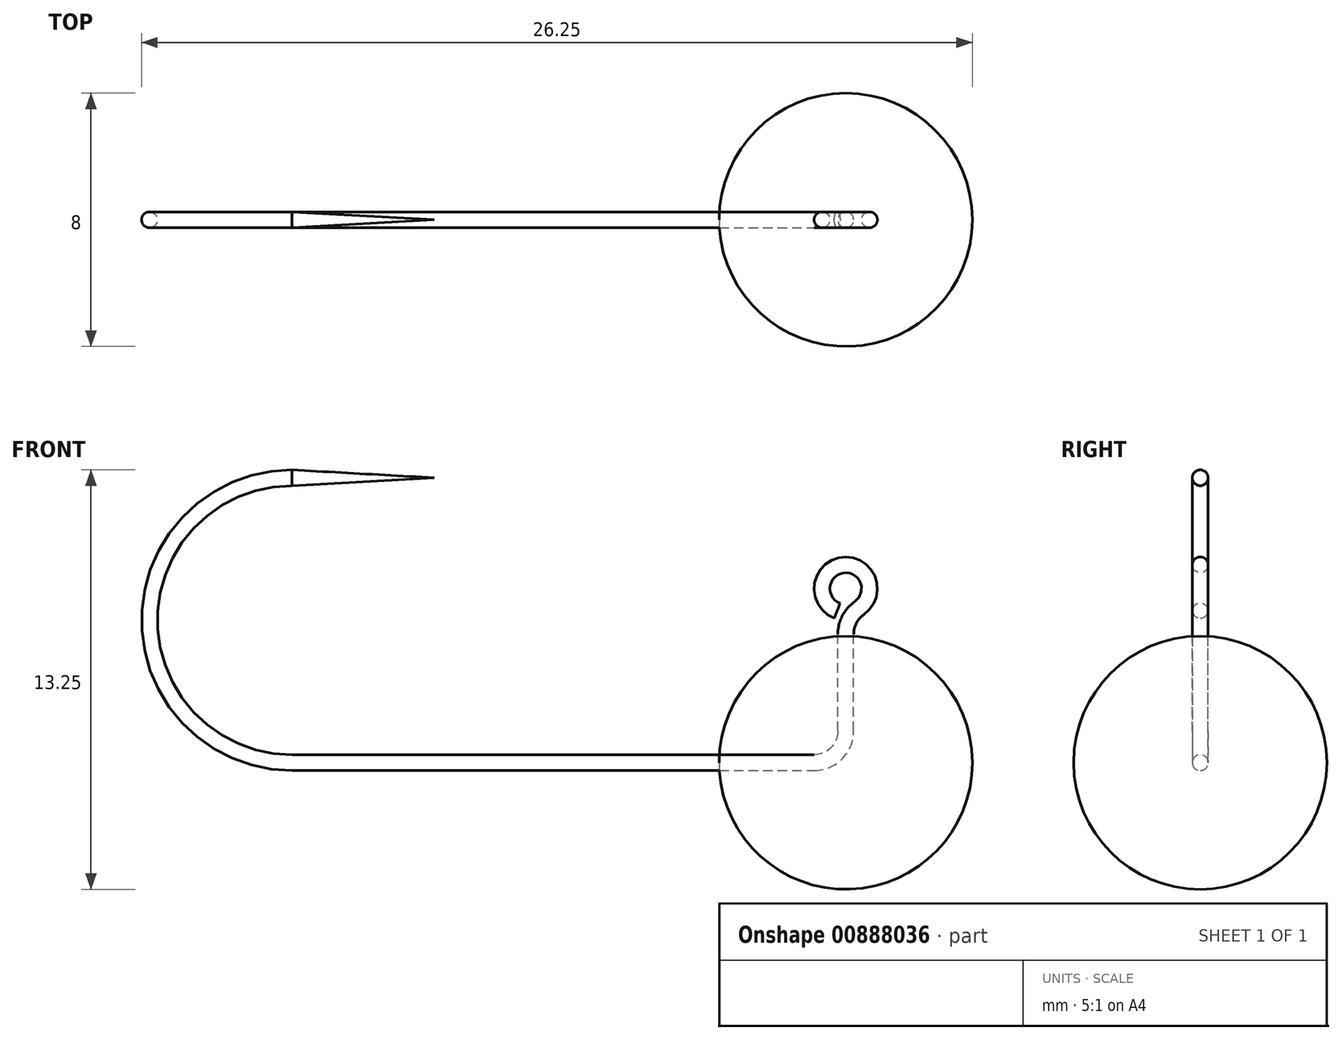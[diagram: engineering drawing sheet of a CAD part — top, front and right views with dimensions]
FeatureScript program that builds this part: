
annotation { "Feature Type Name" : "Feature", "Feature Type Description" : "" }
export const myFeature = defineFeature(function(context is Context, id is Id, definition is map)
    precondition{}
    {
        {
            var Q0;
            Q0=qCreatedBy(makeId("Front.planeOp"),FACE);
            var sketch = newSketch(context, id + "F0", { "sketchPlane" : qUnion([Q0])});
            skArc(sketch, "E0", {"start": v(4, 0) * mm, "mid": v(0, 4) * mm, "end": v(-4, 0) * mm});
            skLineSegment(sketch, "E1", {"start": v(-1, 0) * mm, "end": v(-17.5, 0) * mm});
            skArc(sketch, "E2", {"start": v(-17.5, 0) * mm, "mid": v(-22, 4.5) * mm, "end": v(-17.5, 9) * mm});
            skLineSegment(sketch, "E3", {"start": v(-17.5, 9) * mm, "end": v(-13, 9) * mm});
            skLineSegment(sketch, "E4", {"start": v(0, 1) * mm, "end": v(0, 4.06) * mm});
            skArc(sketch, "E5", {"start": v(0.43, 4.88) * mm, "mid": v(-0.09, 6.24) * mm, "end": v(-0.27, 4.8) * mm});
            skPoint(sketch, "E6.visualSharp", {"position": v(0, 4.75) * mm});
            skArc(sketch, "E6.filletArc", {"start": v(0.43, 4.88) * mm, "mid": v(0.11, 4.53) * mm, "end": v(0, 4.06) * mm});
            skArc(sketch, "E7.filletArc", {"start": v(-1, 0) * mm, "mid": v(-0.3, 0.3) * mm, "end": v(0, 1) * mm});
            skLineSegment(sketch, "E8", {"start": v(-4, 0) * mm, "end": v(4, 0) * mm});
            skSolve(sketch);
        }
        {
            var Q0;
            Q0=makeQuery(id+"F0.imprint","IMPRINT",FACE,{"disambiguationData":[TD([[makeQuery(id+"F0.imprint","IMPRINT",EDGE,{"derivedFrom":sQuery(id+"F0.wireOp",EDGE,"E0")}),1.0]])]});
            var Q1;
            Q1=sQuery(id+"F0.wireOp",EDGE,"E1");
            revolve(context, id + "F1", {"surfaceOperationType" : NewSurfaceOperationType.NEW, "entities" : qUnion([Q0]), "axis" : qUnion([Q1]), "revolveType" : RevolveType.FULL});
        }
        {
            var Q0;
            Q0=qCreatedBy(makeId("Right.planeOp"),FACE);
            var Q1;
            Q1=sQuery(id+"F0.wireOp",VERTEX,"E1.end");
            cPlane(context, id + "F2", {"entities" : qUnion([Q0, Q1]), "cplaneType" : CPlaneType.PLANE_POINT, "offset" : 25 * mm, "width" : 150 * mm, "height" : 150 * mm});
        }
        {
            var Q0;
            Q0=qCreatedBy(id+"F2.planeOp",FACE);
            var sketch = newSketch(context, id + "F3", { "sketchPlane" : qUnion([Q0])});
            skCircle(sketch, "E9", {"center": v(0, 0) * mm, "radius": 0.25 * mm});
            skSolve(sketch);
        }
        {
            var Q0;
            Q0=makeQuery(id+"F3.imprint","IMPRINT",FACE,{"disambiguationData":[TD([[makeQuery(id+"F3.imprint","IMPRINT",EDGE,{"derivedFrom":sQuery(id+"F3.wireOp",EDGE,"E9")}),1.0]])]});
            var Q1;
            Q1=sQuery(id+"F0.wireOp",EDGE,"E3");
            var Q2;
            Q2=sQuery(id+"F0.wireOp",EDGE,"E2");
            var Q3;
            Q3=sQuery(id+"F0.wireOp",EDGE,"E1");
            var Q4;
            Q4=sQuery(id+"F0.wireOp",EDGE,"E7.filletArc");
            var Q5;
            Q5=sQuery(id+"F0.wireOp",EDGE,"E4");
            var Q6;
            Q6=sQuery(id+"F0.wireOp",EDGE,"E6.filletArc");
            var Q7;
            Q7=sQuery(id+"F0.wireOp",EDGE,"E5");
            sweep(context, id + "F4", {"profiles" : qUnion([Q0]), "path" : qUnion([Q1, Q2, Q3, Q4, Q5, Q6, Q7])});
        }
        {
            var Q0;
            Q0=makeQuery(id+"F4.opSweep","CAP_EDGE",EDGE,{"disambiguationData":[OSD([sQuery(id+"F0.wireOp",VERTEX,"E3.end"),sQuery(id+"F3.wireOp",EDGE,"E9")])],"isStart":true});
            chamfer(context, id + "F5", {"entities" : qUnion([Q0]), "chamferType" : ChamferType.TWO_OFFSETS, "width1" : 4.5 * mm, "oppositeDirection" : false, "width2" : 0.25 * mm, "tangentPropagation" : true});
        }
    });
